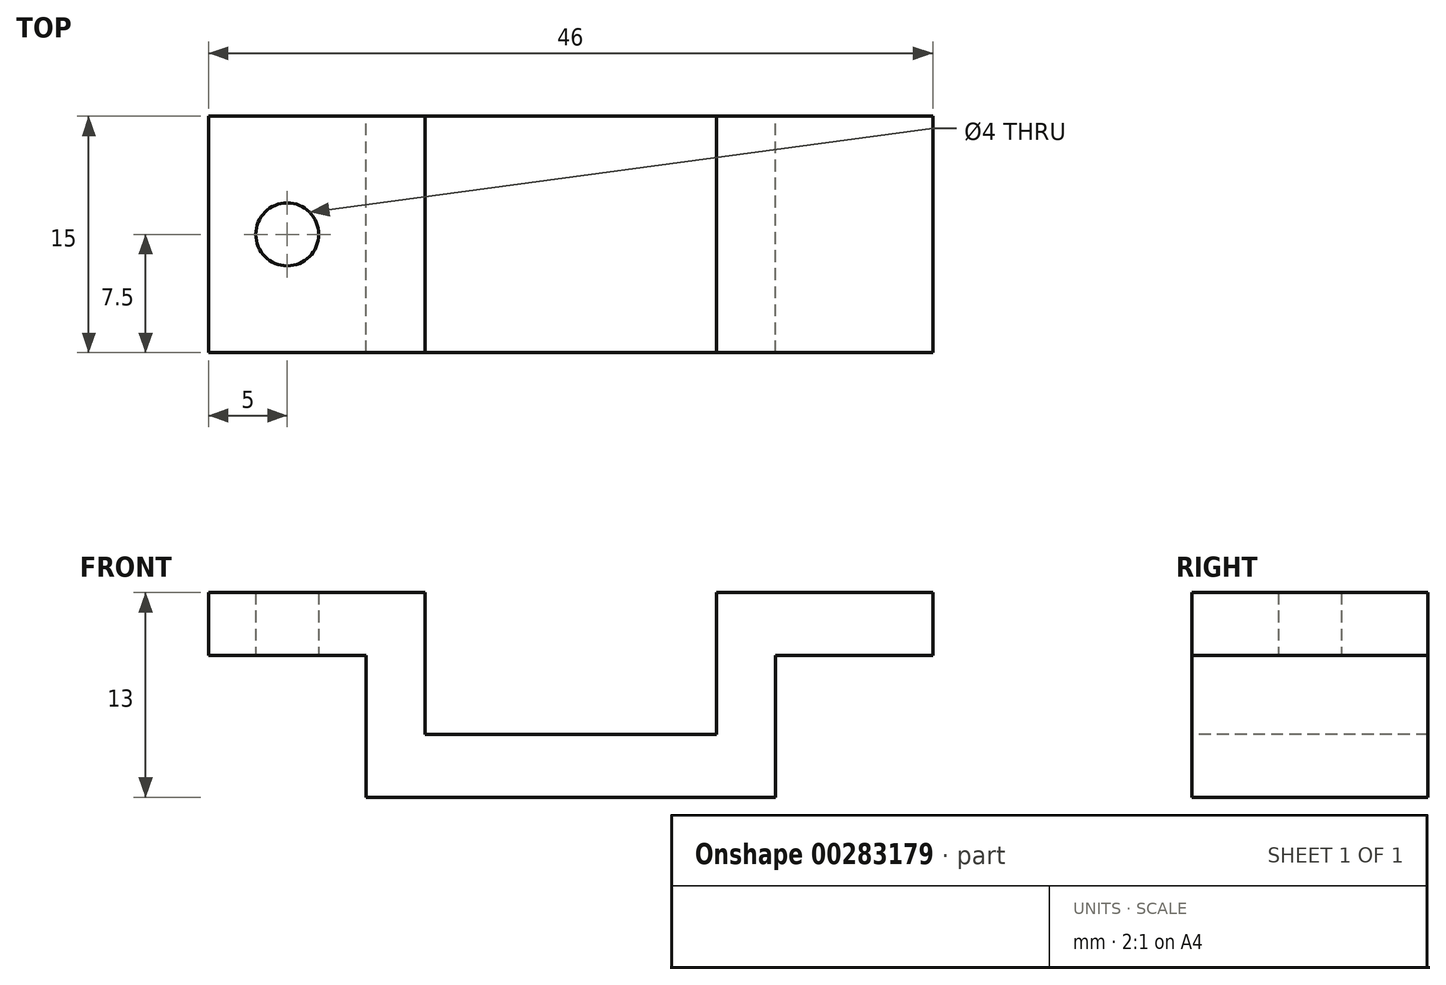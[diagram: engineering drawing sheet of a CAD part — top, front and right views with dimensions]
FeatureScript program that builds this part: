
annotation { "Feature Type Name" : "Feature", "Feature Type Description" : "" }
export const myFeature = defineFeature(function(context is Context, id is Id, definition is map)
    precondition{}
    {
        {
            var Q0;
            Q0=qCreatedBy(makeId("Top.planeOp"),FACE);
            var sketch = newSketch(context, id + "F0", { "sketchPlane" : qUnion([Q0])});
            skLineSegment(sketch, "E0.bottom", {"start": v(-23, 7.5) * mm, "end": v(23, 7.5) * mm});
            skLineSegment(sketch, "E0.top", {"start": v(-23, -7.5) * mm, "end": v(23, -7.5) * mm});
            skLineSegment(sketch, "E0.left", {"start": v(-23, 7.5) * mm, "end": v(-23, -7.5) * mm});
            skLineSegment(sketch, "E0.right", {"start": v(23, 7.5) * mm, "end": v(23, -7.5) * mm});
            skPoint(sketch, "E0.middle", {"position": v(0, 0) * mm});
            skSolve(sketch);
        }
        {
            var Q0;
            Q0=makeQuery(id+"F0.imprint","IMPRINT",FACE,{"disambiguationData":[TD([[makeQuery(id+"F0.imprint","IMPRINT",EDGE,{"derivedFrom":sQuery(id+"F0.wireOp",EDGE,"E0.bottom")}),-1.0]])]});
            extrude(context, id + "F1", {"entities" : qUnion([Q0]), "depth" : 13 * mm});
        }
        {
            var Q0;
            Q0=makeQuery(id+"F1.opExtrude","CAP_FACE",FACE,{"disambiguationData":[OSD([sQuery(id+"F0.wireOp",EDGE,"E0.bottom"),sQuery(id+"F0.wireOp",EDGE,"E0.top"),sQuery(id+"F0.wireOp",EDGE,"E0.left"),sQuery(id+"F0.wireOp",EDGE,"E0.right")])],"isStart":false});
            var sketch = newSketch(context, id + "F2", { "sketchPlane" : qUnion([Q0])});
            skLineSegment(sketch, "E1.bottom", {"start": v(-9.25, 7.5) * mm, "end": v(9.25, 7.5) * mm});
            skLineSegment(sketch, "E1.top", {"start": v(-9.25, -7.5) * mm, "end": v(9.25, -7.5) * mm});
            skLineSegment(sketch, "E1.left", {"start": v(-9.25, 7.5) * mm, "end": v(-9.25, -7.5) * mm});
            skLineSegment(sketch, "E1.right", {"start": v(9.25, 7.5) * mm, "end": v(9.25, -7.5) * mm});
            skPoint(sketch, "E1.middle", {"position": v(0, 0) * mm});
            skSolve(sketch);
        }
        {
            var Q0;
            Q0 = qSketchRegion(id + "F2", true);
            extrude(context, id + "F3", {"entities" : qUnion([Q0]), "operationType" : NewBodyOperationType.REMOVE, "oppositeDirection" : true, "depth" : 9 * mm});
        }
        {
            var Q0;
            Q0=makeQuery(id+"F1.opExtrude","CAP_FACE",FACE,{"disambiguationData":[OSD([sQuery(id+"F0.wireOp",EDGE,"E0.bottom"),sQuery(id+"F0.wireOp",EDGE,"E0.top"),sQuery(id+"F0.wireOp",EDGE,"E0.left"),sQuery(id+"F0.wireOp",EDGE,"E0.right")])],"isStart":true});
            var sketch = newSketch(context, id + "F4", { "sketchPlane" : qUnion([Q0])});
            skLineSegment(sketch, "E2.bottom", {"start": v(-23, 7.5) * mm, "end": v(-13, 7.5) * mm});
            skLineSegment(sketch, "E2.top", {"start": v(-23, -7.5) * mm, "end": v(-13, -7.5) * mm});
            skLineSegment(sketch, "E2.left", {"start": v(-23, 7.5) * mm, "end": v(-23, -7.5) * mm});
            skLineSegment(sketch, "E2.right", {"start": v(-13, 7.5) * mm, "end": v(-13, -7.5) * mm});
            skLineSegment(sketch, "E3.MirrorCS", {"start": v(23, 7.5) * mm, "end": v(13, 7.5) * mm});
            skLineSegment(sketch, "E4.MirrorCS", {"start": v(13, 7.5) * mm, "end": v(13, -7.5) * mm});
            skLineSegment(sketch, "E5.MirrorCS", {"start": v(23, 7.5) * mm, "end": v(23, -7.5) * mm});
            skLineSegment(sketch, "E6.MirrorCS", {"start": v(23, -7.5) * mm, "end": v(13, -7.5) * mm});
            skSolve(sketch);
        }
        {
            var Q0;
            Q0=makeQuery(id+"F4.imprint","IMPRINT",FACE,{"disambiguationData":[TD([[makeQuery(id+"F4.imprint","IMPRINT",EDGE,{"derivedFrom":sQuery(id+"F4.wireOp",EDGE,"E2.bottom")}),-1.0]])]});
            var Q1;
            Q1=makeQuery(id+"F4.imprint","IMPRINT",FACE,{"disambiguationData":[TD([[makeQuery(id+"F4.imprint","IMPRINT",EDGE,{"derivedFrom":sQuery(id+"F4.wireOp",EDGE,"E3.MirrorCS")}),-1.0]])]});
            var Q2;
            Q2=sQuery(id+"F4.wireOp",EDGE,"E2.right");
            var Q3;
            Q3=sQuery(id+"F4.wireOp",EDGE,"E2.bottom");
            var Q4;
            Q4=sQuery(id+"F4.wireOp",EDGE,"E2.top");
            var Q5;
            Q5=sQuery(id+"F4.wireOp",EDGE,"E2.left");
            var Q6;
            Q6=sQuery(id+"F4.wireOp",EDGE,"E4.MirrorCS");
            var Q7;
            Q7=sQuery(id+"F4.wireOp",EDGE,"E3.MirrorCS");
            var Q8;
            Q8=sQuery(id+"F4.wireOp",EDGE,"E6.MirrorCS");
            var Q9;
            Q9=sQuery(id+"F4.wireOp",EDGE,"E5.MirrorCS");
            extrude(context, id + "F5", {"entities" : qUnion([Q0, Q1]), "operationType" : NewBodyOperationType.REMOVE, "surfaceEntities" : qUnion([Q2, Q3, Q4, Q5, Q6, Q7, Q8, Q9]), "oppositeDirection" : true, "depth" : 9 * mm});
        }
        {
            var Q0;
            Q0=makeQuery(id+"F5.boolean.opBoolean","COPY",FACE,{"derivedFrom":makeQuery(id+"F5.opExtrude","CAP_FACE",FACE,{"disambiguationData":[OSD([sQuery(id+"F4.wireOp",EDGE,"E2.bottom"),sQuery(id+"F4.wireOp",EDGE,"E2.top"),sQuery(id+"F4.wireOp",EDGE,"E2.left"),sQuery(id+"F4.wireOp",EDGE,"E2.right")])],"isStart":false})});
            var sketch = newSketch(context, id + "F6", { "sketchPlane" : qUnion([Q0])});
            skCircle(sketch, "E7", {"center": v(-18, 0) * mm, "radius": 2 * mm});
            skPoint(sketch, "E7.centerSnap0", {"position": v(-18, 7.5) * mm});
            skCircle(sketch, "E8.MirrorC", {"center": v(18, 0) * mm, "radius": 2 * mm});
            skSolve(sketch);
        }
        {
            var Q0;
            Q0=makeQuery(id+"F6.imprint","IMPRINT",FACE,{"disambiguationData":[TD([[makeQuery(id+"F6.imprint","IMPRINT",EDGE,{"derivedFrom":sQuery(id+"F6.wireOp",EDGE,"E7")}),1.0]])]});
            var Q1;
            Q1=makeQuery(id+"F6.imprint","IMPRINT",FACE,{"disambiguationData":[TD([[makeQuery(id+"F6.imprint","IMPRINT",EDGE,{"derivedFrom":sQuery(id+"F6.wireOp",EDGE,"E8.MirrorC")}),-1.0]])]});
            var Q2;
            Q2=sQuery(id+"F6.wireOp",EDGE,"E7");
            var Q3;
            Q3=sQuery(id+"F6.wireOp",EDGE,"E8.MirrorC");
            extrude(context, id + "F7", {"entities" : qUnion([Q0, Q1]), "operationType" : NewBodyOperationType.REMOVE, "surfaceEntities" : qUnion([Q2, Q3]), "oppositeDirection" : true, "depth" : 25 * mm});
        }
    });
